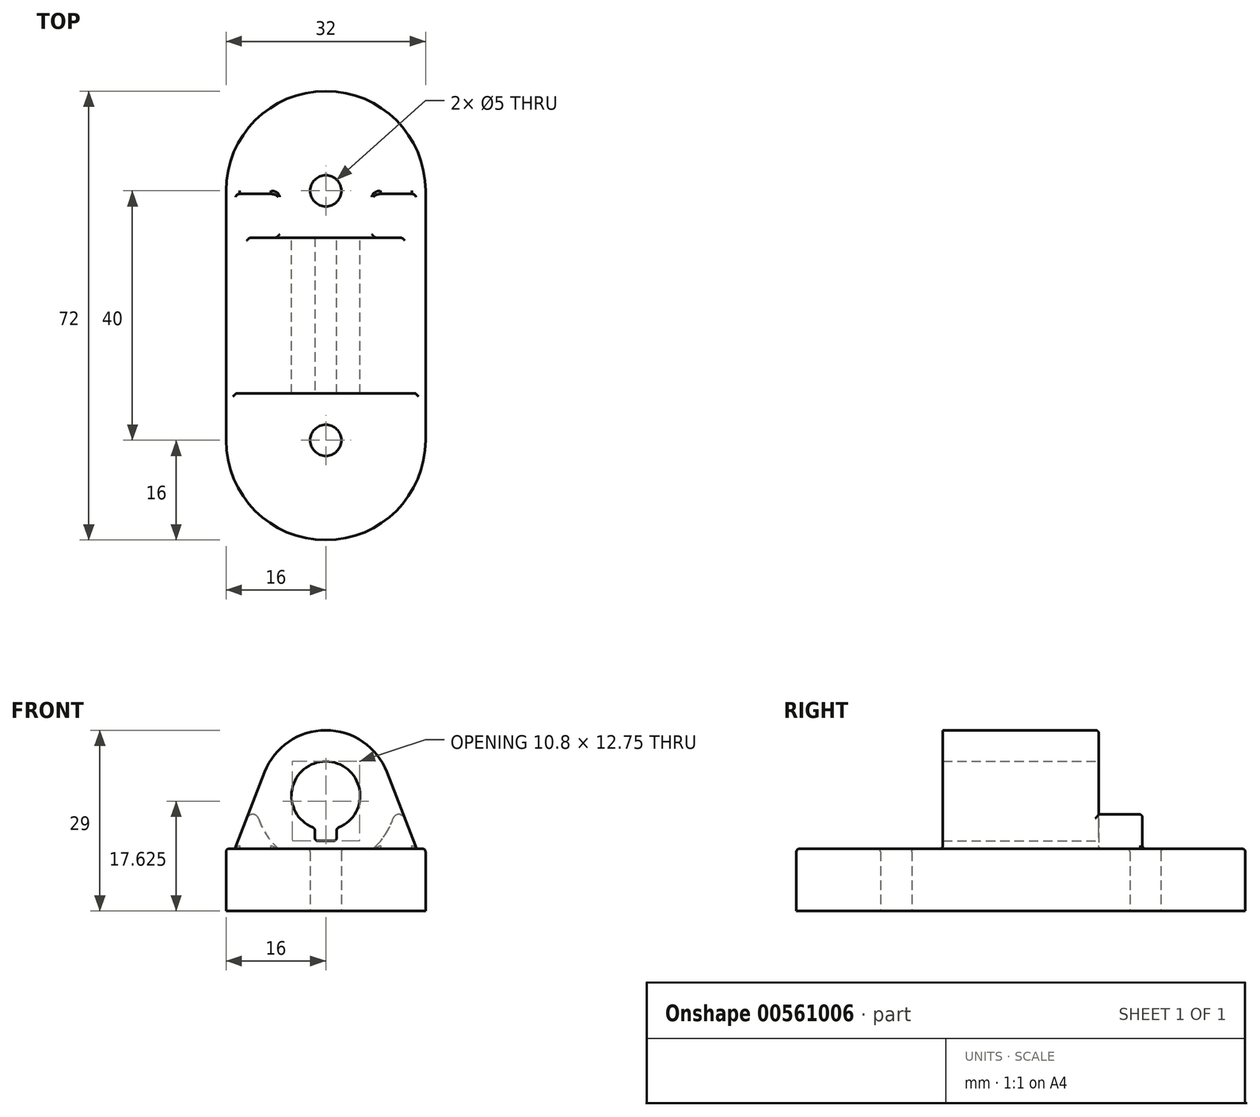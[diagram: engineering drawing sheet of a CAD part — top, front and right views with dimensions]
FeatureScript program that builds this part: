
annotation { "Feature Type Name" : "Feature", "Feature Type Description" : "" }
export const myFeature = defineFeature(function(context is Context, id is Id, definition is map)
    precondition{}
    {
        {
            var Q0;
            Q0=qCreatedBy(makeId("Top.planeOp"),FACE);
            var sketch = newSketch(context, id + "F0", { "sketchPlane" : qUnion([Q0])});
            skCircle(sketch, "E0", {"center": v(0, 20) * mm, "radius": 2.5 * mm});
            skCircle(sketch, "E1.MirrorC", {"center": v(0, -20) * mm, "radius": 2.5 * mm});
            skArc(sketch, "E2", {"start": v(16, 20) * mm, "mid": v(0, 36) * mm, "end": v(-16, 20) * mm});
            skArc(sketch, "E3.MirrorC", {"start": v(16, -20) * mm, "mid": v(0, -36) * mm, "end": v(-16, -20) * mm});
            skLineSegment(sketch, "E4", {"start": v(-16, 20) * mm, "end": v(-16, -20) * mm});
            skLineSegment(sketch, "E5.MirrorCS", {"start": v(16, 20) * mm, "end": v(16, -20) * mm});
            skSolve(sketch);
        }
        {
            var Q0;
            Q0 = qSketchRegion(id + "F0", true);
            extrude(context, id + "F1", {"entities" : qUnion([Q0]), "depth" : 10 * mm, "offsetDistance" : 25 * mm});
        }
        {
            var Q0;
            Q0=qCreatedBy(makeId("Front.planeOp"),FACE);
            var sketch = newSketch(context, id + "F2", { "sketchPlane" : qUnion([Q0])});
            skArc(sketch, "E6", {"start": v(1.75, 13.29) * mm, "mid": v(0, 24) * mm, "end": v(-1.75, 13.29) * mm});
            skArc(sketch, "E7.0", {"start": v(9.79, 22.3) * mm, "mid": v(0, 29) * mm, "end": v(-9.79, 22.3) * mm});
            skLineSegment(sketch, "E8", {"start": v(10.5, 9.25) * mm, "end": v(-10.5, 9.25) * mm});
            skPoint(sketch, "E9.orphan", {"position": v(-10.5, 0) * mm});
            skPoint(sketch, "E10.orphan", {"position": v(10.5, 0) * mm});
            skLineSegment(sketch, "E11.bottom", {"start": v(1.75, 11.25) * mm, "end": v(-1.75, 11.25) * mm});
            skLineSegment(sketch, "E11.left", {"start": v(1.75, 11.25) * mm, "end": v(1.75, 13.29) * mm});
            skLineSegment(sketch, "E11.right", {"start": v(-1.75, 11.25) * mm, "end": v(-1.75, 13.29) * mm});
            skPoint(sketch, "E11.middle", {"position": v(0, 13) * mm});
            skPoint(sketch, "E12.orphan", {"position": v(-1.75, 14.75) * mm});
            skPoint(sketch, "E13.orphan", {"position": v(1.75, 14.75) * mm});
            skLineSegment(sketch, "E14", {"start": v(10.5, 9.25) * mm, "end": v(14.85, 9.25) * mm});
            skLineSegment(sketch, "E15", {"start": v(14.85, 9.25) * mm, "end": v(9.79, 22.3) * mm});
            skPoint(sketch, "E16.orphan", {"position": v(10.5, 18.5) * mm});
            skLineSegment(sketch, "E17.MirrorCS", {"start": v(-14.85, 9.25) * mm, "end": v(-9.79, 22.3) * mm});
            skLineSegment(sketch, "E18.MirrorCS", {"start": v(-10.5, 9.25) * mm, "end": v(-14.85, 9.25) * mm});
            skPoint(sketch, "E19.orphan", {"position": v(-10.5, 18.5) * mm});
            skSolve(sketch);
        }
        {
            var Q0;
            Q0=makeQuery(id+"F2.imprint","IMPRINT",FACE,{"disambiguationData":[TD([[makeQuery(id+"F2.imprint","IMPRINT",EDGE,{"derivedFrom":sQuery(id+"F2.wireOp",EDGE,"E6")}),-1.0]])]});
            extrude(context, id + "F3", {"entities" : qUnion([Q0]), "operationType" : NewBodyOperationType.ADD, "endBound" : BoundingType.SYMMETRIC, "depth" : 25 * mm, "offsetDistance" : 25 * mm});
        }
        {
            var Q0;
            Q0=makeQuery(id+"F3.opExtrude","SWEPT_EDGE",EDGE,{"disambiguationData":[OSD([sQuery(id+"F2.wireOp",EDGE,"E11.bottom"),sQuery(id+"F2.wireOp",EDGE,"E11.right")])]});
            var Q1;
            Q1=makeQuery(id+"F3.opExtrude","SWEPT_EDGE",EDGE,{"disambiguationData":[OSD([sQuery(id+"F2.wireOp",EDGE,"E11.bottom"),sQuery(id+"F2.wireOp",EDGE,"E11.left")])]});
            var Q2;
            Q2=makeQuery(id+"F3.opExtrude","SWEPT_EDGE",EDGE,{"disambiguationData":[OSD([sQuery(id+"F2.wireOp",EDGE,"E6"),sQuery(id+"F2.wireOp",EDGE,"E11.left")])]});
            var Q3;
            Q3=makeQuery(id+"F3.opExtrude","SWEPT_EDGE",EDGE,{"disambiguationData":[OSD([sQuery(id+"F2.wireOp",EDGE,"E6"),sQuery(id+"F2.wireOp",EDGE,"E11.right")])]});
            fillet(context, id + "F4", {"entities" : qUnion([Q0, Q1, Q2, Q3]), "radius" : .5 * mm, "tangentPropagation" : true, "allowEdgeOverflow" : false});
        }
        {
            var Q0;
            Q0=makeQuery(id+"F3.opExtrude","CAP_FACE",FACE,{"disambiguationData":[OSD([sQuery(id+"F2.wireOp",EDGE,"E6"),sQuery(id+"F2.wireOp",EDGE,"E7.0"),sQuery(id+"F2.wireOp",EDGE,"E8"),sQuery(id+"F2.wireOp",EDGE,"E11.bottom"),sQuery(id+"F2.wireOp",EDGE,"E11.left"),sQuery(id+"F2.wireOp",EDGE,"E11.right"),sQuery(id+"F2.wireOp",EDGE,"E14"),sQuery(id+"F2.wireOp",EDGE,"E15"),sQuery(id+"F2.wireOp",EDGE,"E17.MirrorCS"),sQuery(id+"F2.wireOp",EDGE,"E18.MirrorCS")])],"isStart":true});
            var sketch = newSketch(context, id + "F5", { "sketchPlane" : qUnion([Q0])});
            skArc(sketch, "E20", {"start": v(-11.4, 18.17) * mm, "mid": v(-10.33, 13.7) * mm, "end": v(-7.59, 10) * mm});
            skLineSegment(sketch, "E21", {"start": v(-7.59, 10) * mm, "end": v(-14.56, 10) * mm});
            skLineSegment(sketch, "E22", {"start": v(-14.56, 10) * mm, "end": v(-11.4, 18.17) * mm});
            skLineSegment(sketch, "E23", {"start": v(14.56, 10) * mm, "end": v(7.59, 10) * mm});
            skLineSegment(sketch, "E24", {"start": v(14.56, 10) * mm, "end": v(11.4, 18.17) * mm});
            skArc(sketch, "E25.trimOffspring", {"start": v(7.59, 10) * mm, "mid": v(10.33, 13.7) * mm, "end": v(11.4, 18.17) * mm});
            skSolve(sketch);
        }
        {
            var Q0;
            Q0=makeQuery(id+"F5.imprint","IMPRINT",FACE,{"disambiguationData":[TD([[makeQuery(id+"F5.imprint","IMPRINT",EDGE,{"derivedFrom":sQuery(id+"F5.wireOp",EDGE,"E23")}),-1.0]])]});
            var Q1;
            Q1=makeQuery(id+"F5.imprint","IMPRINT",FACE,{"disambiguationData":[TD([[makeQuery(id+"F5.imprint","IMPRINT",EDGE,{"derivedFrom":sQuery(id+"F5.wireOp",EDGE,"E20")}),-1.0]])]});
            extrude(context, id + "F6", {"entities" : qUnion([Q0, Q1]), "operationType" : NewBodyOperationType.ADD, "depth" : 7 * mm, "offsetDistance" : 25 * mm});
        }
        {
            var Q0;
            Q0=makeQuery(id+"F6.opExtrude","SWEPT_EDGE",EDGE,{"disambiguationData":[OSD([sQuery(id+"F2.wireOp",EDGE,"E17.MirrorCS"),sQuery(id+"F5.wireOp",EDGE,"E24"),sQuery(id+"F5.wireOp",EDGE,"E25.trimOffspring")])]});
            var Q1;
            Q1=makeQuery(id+"F6.opExtrude","SWEPT_EDGE",EDGE,{"disambiguationData":[OSD([sQuery(id+"F2.wireOp",EDGE,"E15"),sQuery(id+"F5.wireOp",EDGE,"E20"),sQuery(id+"F5.wireOp",EDGE,"E22")])]});
            fillet(context, id + "F7", {"entities" : qUnion([Q0, Q1]), "radius" : 1 * mm, "tangentPropagation" : true, "allowEdgeOverflow" : false});
        }
        {
            var Q0;
            Q0=makeQuery(id+"F1.opExtrude","CAP_FACE",FACE,{"disambiguationData":[OSD([sQuery(id+"F0.wireOp",EDGE,"E0"),sQuery(id+"F0.wireOp",EDGE,"E1.MirrorC"),sQuery(id+"F0.wireOp",EDGE,"E2"),sQuery(id+"F0.wireOp",EDGE,"E3.MirrorC"),sQuery(id+"F0.wireOp",EDGE,"E4"),sQuery(id+"F0.wireOp",EDGE,"E5.MirrorCS")])],"isStart":false});
            var Q1;
            Q1=makeQuery(id+"F6.opExtrude","CAP_EDGE",EDGE,{"disambiguationData":[OSD([sQuery(id+"F5.wireOp",EDGE,"E23")])],"isStart":false});
            var Q2;
            Q2=makeQuery(id+"F6.opExtrude","CAP_EDGE",EDGE,{"disambiguationData":[OSD([sQuery(id+"F5.wireOp",EDGE,"E25.trimOffspring")])],"isStart":false});
            var Q3;
            Q3=makeQuery(id+"F6.opExtrude","CAP_EDGE",EDGE,{"disambiguationData":[OSD([sQuery(id+"F5.wireOp",EDGE,"E24")])],"isStart":false});
            var Q4;
            Q4=makeQuery(id+"F6.opExtrude","CAP_EDGE",EDGE,{"disambiguationData":[OSD([sQuery(id+"F5.wireOp",EDGE,"E22")])],"isStart":false});
            var Q5;
            {var subQ0=sQuery(id+"F5.wireOp",EDGE,"E22");var subQ1=sQuery(id+"F5.wireOp",EDGE,"E20");Q5=makeQuery(id+"F7.opFillet","BLEND_EDGE",EDGE,{"blendedFrom":[makeQuery(id+"F6.opExtrude","SWEPT_EDGE",EDGE,{"disambiguationData":[OSD([sQuery(id+"F2.wireOp",EDGE,"E15"),subQ1,subQ0])]}),makeQuery(id+"F6.opExtrude","CAP_FACE",FACE,{"disambiguationData":[OSD([subQ1,sQuery(id+"F5.wireOp",EDGE,"E21"),subQ0])],"isStart":false})],"blendedInto":[makeQuery(id+"F6.opExtrude","CAP_FACE",FACE,{"disambiguationData":[OSD([subQ1,sQuery(id+"F5.wireOp",EDGE,"E21"),subQ0])],"isStart":false})]});}
            var Q6;
            Q6=makeQuery(id+"F6.opExtrude","CAP_EDGE",EDGE,{"disambiguationData":[OSD([sQuery(id+"F5.wireOp",EDGE,"E20")])],"isStart":false});
            var Q7;
            Q7=makeQuery(id+"F3.opExtrude","CAP_EDGE",EDGE,{"disambiguationData":[OSD([sQuery(id+"F2.wireOp",EDGE,"E15")])],"isStart":true});
            var Q8;
            Q8=makeQuery(id+"F3.opExtrude","CAP_EDGE",EDGE,{"disambiguationData":[OSD([sQuery(id+"F2.wireOp",EDGE,"E7.0")])],"isStart":true});
            fillet(context, id + "F8", {"entities" : qUnion([Q0, Q1, Q2, Q3, Q4, Q5, Q6, Q7, Q8]), "radius" : .5 * mm, "tangentPropagation" : true, "allowEdgeOverflow" : false});
        }
    });
